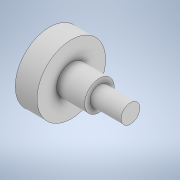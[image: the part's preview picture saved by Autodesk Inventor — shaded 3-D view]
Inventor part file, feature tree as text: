
AUTODESK INVENTOR PART (.ipt)
format: ipt  version: 2020 (Build 240168000, 168)  size: 112,640 bytes
history: native  units: mm
features: revolve x1, sketch x1
ambient origin geometry x8: Origin, YZ Plane, XZ Plane, XY Plane, X Axis, Y Axis, Z Axis, Center Point
bodies: Solid1 (feature_tree)
feature tree (2):
  revolve  "Revolution1"  Angle=90.0deg
  sketch  "Sketch1"  dims[d3=9.0mm d4=90.0deg d5=11.0mm d6=7.0mm d7=1.75mm d8=3.0mm d9=4.75mm]
